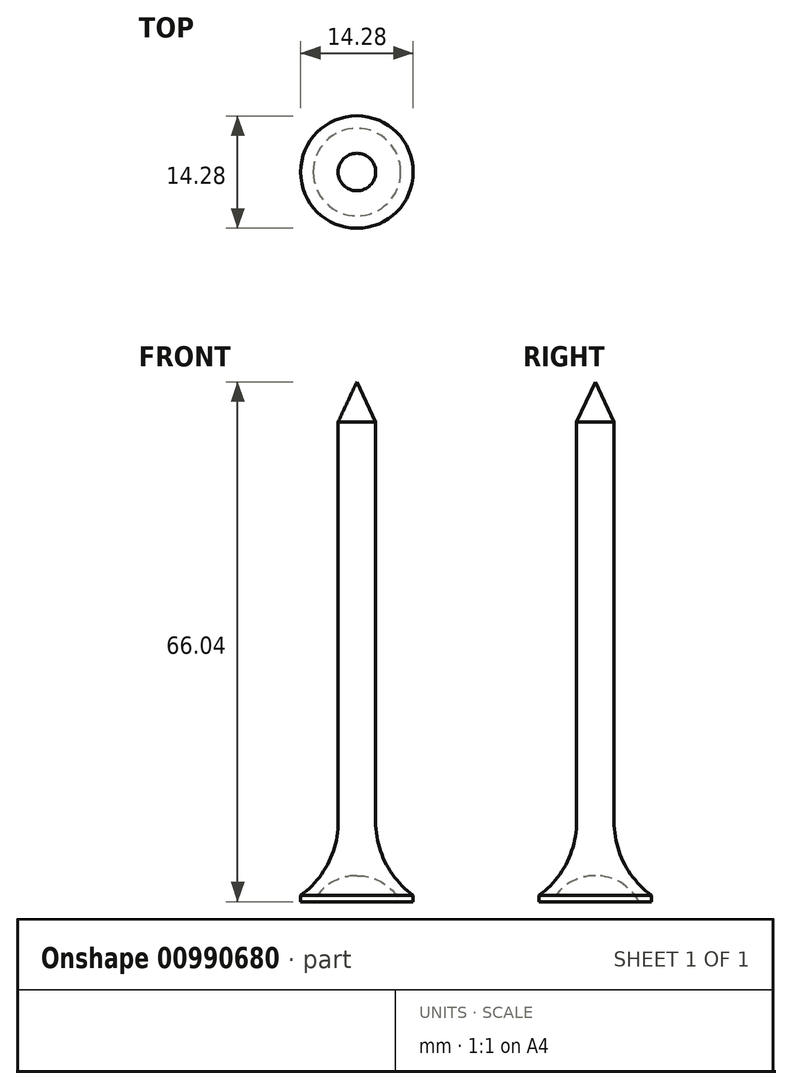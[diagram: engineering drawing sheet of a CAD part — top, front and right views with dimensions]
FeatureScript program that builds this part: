
annotation { "Feature Type Name" : "Feature", "Feature Type Description" : "" }
export const myFeature = defineFeature(function(context is Context, id is Id, definition is map)
    precondition{}
    {
        {
            var Q0;
            Q0=qCreatedBy(makeId("Front.planeOp"),FACE);
            var sketch = newSketch(context, id + "F0", { "sketchPlane" : qUnion([Q0])});
            skLineSegment(sketch, "E0", {"start": v(0, 0) * mm, "end": v(5.56, 0) * mm, "construction": true});
            skLineSegment(sketch, "E1", {"start": v(5.56, 0) * mm, "end": v(7.14, 0) * mm});
            skLineSegment(sketch, "E2", {"start": v(0, 0) * mm, "end": v(0, 3.3) * mm, "construction": true});
            skArc(sketch, "E3", {"start": v(5.56, 0) * mm, "mid": v(3.23, 2.41) * mm, "end": v(0, 3.3) * mm});
            skLineSegment(sketch, "E4.bottom", {"start": v(0, 0) * mm, "end": v(2.38, 0) * mm, "construction": true});
            skLineSegment(sketch, "E4.top", {"start": v(0, 10.16) * mm, "end": v(2.38, 10.16) * mm, "construction": true});
            skLineSegment(sketch, "E4.left", {"start": v(0, 0) * mm, "end": v(0, 10.16) * mm, "construction": true});
            skLineSegment(sketch, "E4.right", {"start": v(2.38, 0) * mm, "end": v(2.38, 10.16) * mm, "construction": true});
            skLineSegment(sketch, "E5", {"start": v(2.38, 10.16) * mm, "end": v(2.38, 60.96) * mm});
            skLineSegment(sketch, "E6", {"start": v(0, 0) * mm, "end": v(0, 66.04) * mm});
            skPoint(sketch, "E6.endSnap0", {"position": v(0, 5.08) * mm});
            skLineSegment(sketch, "E7", {"start": v(2.38, 60.96) * mm, "end": v(0, 66.04) * mm});
            skLineSegment(sketch, "E8", {"start": v(0, 0) * mm, "end": v(0, 100.57) * mm, "construction": true});
            skPoint(sketch, "E8.endSnap0", {"position": v(0, 33.02) * mm});
            skLineSegment(sketch, "E9", {"start": v(7.14, 0) * mm, "end": v(7.14, 0.8) * mm});
            skArc(sketch, "E10", {"start": v(2.38, 10.16) * mm, "mid": v(3.64, 4.9) * mm, "end": v(7.14, 0.8) * mm});
            skSolve(sketch);
        }
        {
            var Q0;
            Q0=qSketchRegion(id+"F0",true);
            var Q1;
            Q1=sQuery(id+"F0.wireOp",EDGE,"E8");
            revolve(context, id + "F1", {"entities" : qUnion([Q0]), "axis" : qUnion([Q1]), "revolveType" : RevolveType.FULL});
        }
    });
